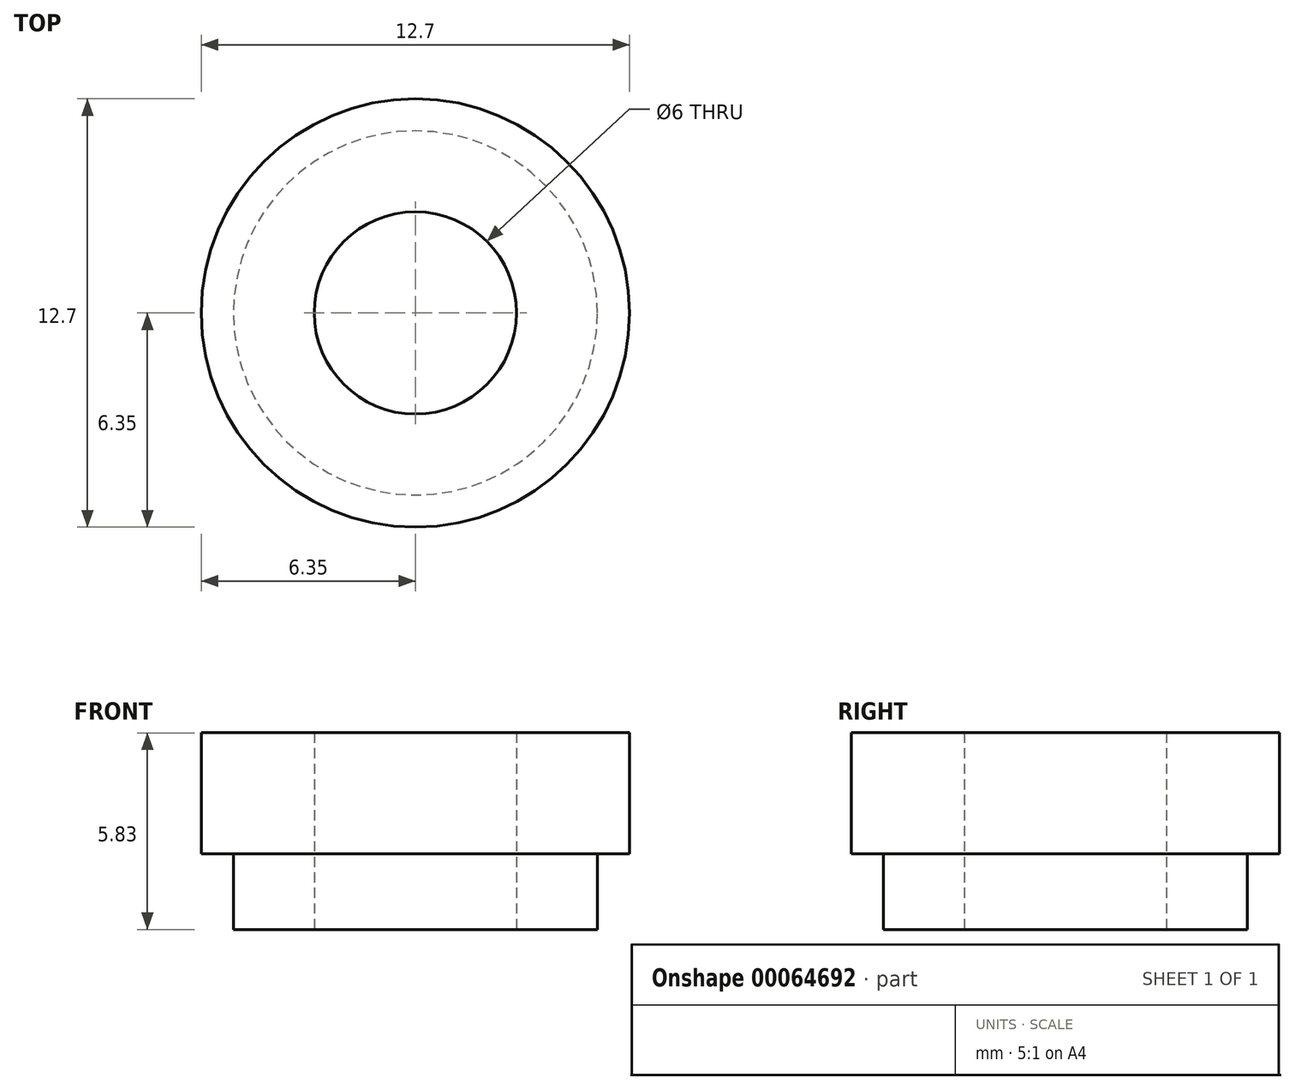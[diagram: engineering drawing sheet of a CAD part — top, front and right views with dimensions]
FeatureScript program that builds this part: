
annotation { "Feature Type Name" : "Feature", "Feature Type Description" : "" }
export const myFeature = defineFeature(function(context is Context, id is Id, definition is map)
    precondition{}
    {
        {
            var Q0;
            Q0=qCreatedBy(makeId("Top.planeOp"),FACE);
            var sketch = newSketch(context, id + "F0", { "sketchPlane" : qUnion([Q0])});
            skCircle(sketch, "E0", {"center": v(0, 0) * mm, "radius": 12.7 * mm});
            skSolve(sketch);
        }
        {
            var Q0;
            Q0 = qSketchRegion(id + "F0", true);
            extrude(context, id + "F1", {"entities" : qUnion([Q0]), "depth" : 7.2 * mm});
        }
        {
            var Q0;
            Q0=makeQuery(id+"F0.imprint","IMPRINT",FACE,{"disambiguationData":[TD([[makeQuery(id+"F0.imprint","IMPRINT",EDGE,{"derivedFrom":sQuery(id+"F0.wireOp",EDGE,"E0")}),1.0]])]});
            var sketch = newSketch(context, id + "F2", { "sketchPlane" : qUnion([Q0])});
            skCircle(sketch, "E1", {"center": v(0, 0) * mm, "radius": 10.8 * mm});
            skSolve(sketch);
        }
        {
            var Q0;
            Q0 = qSketchRegion(id + "F2", true);
            extrude(context, id + "F3", {"entities" : qUnion([Q0]), "operationType" : NewBodyOperationType.ADD, "oppositeDirection" : true, "depth" : 4.48 * mm});
        }
        {
            var Q0;
            Q0=makeQuery(id+"F3.opExtrude","CAP_FACE",FACE,{"disambiguationData":[OSD([sQuery(id+"F2.wireOp",EDGE,"E1")])],"isStart":false});
            var sketch = newSketch(context, id + "F4", { "sketchPlane" : qUnion([Q0])});
            skCircle(sketch, "E2", {"center": v(0, 0) * mm, "radius": 6 * mm});
            skSolve(sketch);
        }
        {
            var Q0;
            Q0 = qSketchRegion(id + "F4", true);
            extrude(context, id + "F5", {"entities" : qUnion([Q0]), "operationType" : NewBodyOperationType.REMOVE, "oppositeDirection" : true, "depth" : 25.4 * mm});
        }
        {
            var Q0;
            Q0=makeQuery(id+"F1.opExtrude","SWEPT_BODY",BODY,{"disambiguationData":[OSD([sQuery(id+"F0.wireOp",EDGE,"E0")])]});
            var Q1;
            Q1=qCreatedBy(makeId("Origin.pointOp"),VERTEX);
            transform(context, id + "F6", {"entities" : qUnion([Q0]), "transformType" : TransformType.SCALE_UNIFORMLY, "scale" : .5, "scalePoint" : qUnion([Q1]), "makeCopy" : false});
        }
    });
